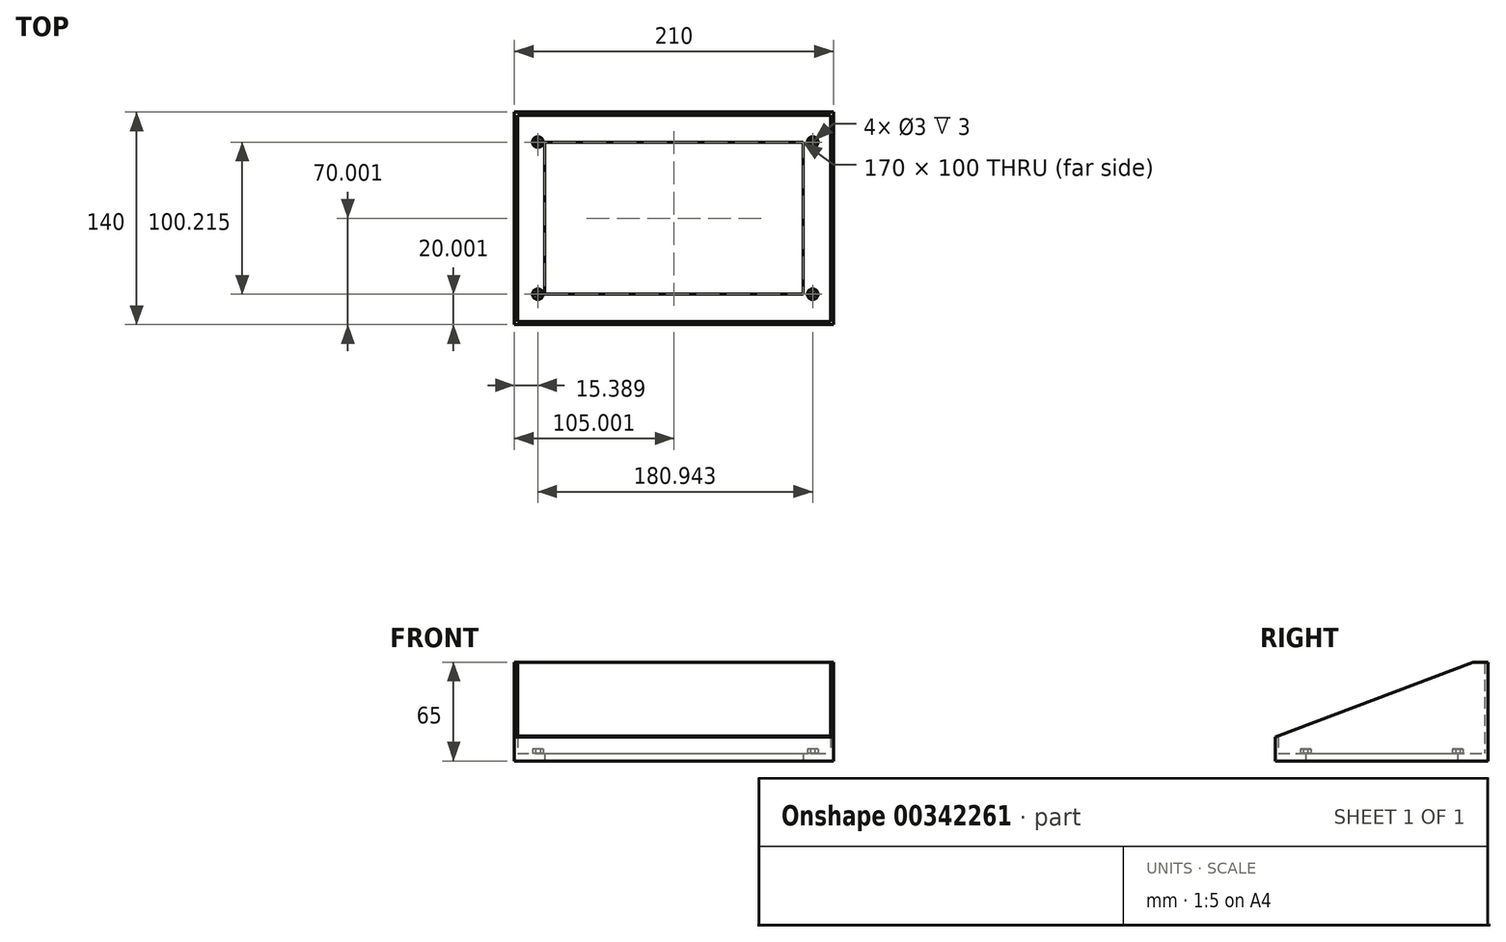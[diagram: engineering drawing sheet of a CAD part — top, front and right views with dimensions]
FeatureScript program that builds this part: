
annotation { "Feature Type Name" : "Feature", "Feature Type Description" : "" }
export const myFeature = defineFeature(function(context is Context, id is Id, definition is map)
    precondition{}
    {
        {
            var Q0;
            Q0=qCreatedBy(makeId("Top.planeOp"),FACE);
            var sketch = newSketch(context, id + "F0", { "sketchPlane" : qUnion([Q0])});
            skLineSegment(sketch, "E0.bottom", {"start": v(-80.08, -50.32) * mm, "end": v(89.92, -50.32) * mm});
            skLineSegment(sketch, "E0.top", {"start": v(-80.08, 49.68) * mm, "end": v(89.92, 49.68) * mm});
            skLineSegment(sketch, "E0.left", {"start": v(-80.08, -50.32) * mm, "end": v(-80.08, 49.68) * mm});
            skLineSegment(sketch, "E0.right", {"start": v(89.92, -50.32) * mm, "end": v(89.92, 49.68) * mm});
            skLineSegment(sketch, "E1.0", {"start": v(-100.08, 69.68) * mm, "end": v(109.92, 69.68) * mm});
            skLineSegment(sketch, "E1.1", {"start": v(-100.08, -70.32) * mm, "end": v(-100.08, 69.68) * mm});
            skLineSegment(sketch, "E1.2", {"start": v(-100.08, -70.32) * mm, "end": v(109.92, -70.32) * mm});
            skLineSegment(sketch, "E1.3", {"start": v(109.92, -70.32) * mm, "end": v(109.92, 69.68) * mm});
            skSolve(sketch);
        }
        {
            var Q0;
            Q0=makeQuery(id+"F0.imprint","IMPRINT",FACE,{"disambiguationData":[TD([[makeQuery(id+"F0.imprint","IMPRINT",EDGE,{"derivedFrom":sQuery(id+"F0.wireOp",EDGE,"E0.bottom")}),-1.0]])]});
            extrude(context, id + "F1", {"entities" : qUnion([Q0]), "depth" : 5 * mm});
        }
        {
            var Q0;
            Q0=makeQuery(id+"F1.opExtrude","CAP_FACE",FACE,{"disambiguationData":[OSD([sQuery(id+"F0.wireOp",EDGE,"E0.bottom"),sQuery(id+"F0.wireOp",EDGE,"E0.top"),sQuery(id+"F0.wireOp",EDGE,"E0.left"),sQuery(id+"F0.wireOp",EDGE,"E0.right"),sQuery(id+"F0.wireOp",EDGE,"E1.0"),sQuery(id+"F0.wireOp",EDGE,"E1.1"),sQuery(id+"F0.wireOp",EDGE,"E1.2"),sQuery(id+"F0.wireOp",EDGE,"E1.3")])],"isStart":false});
            var sketch = newSketch(context, id + "F2", { "sketchPlane" : qUnion([Q0])});
            skPoint(sketch, "E2", {"position": v(-84.7, 49.9) * mm});
            skPoint(sketch, "E3", {"position": v(96.25, 49.9) * mm});
            skPoint(sketch, "E4", {"position": v(96.25, -50.32) * mm});
            skPoint(sketch, "E5", {"position": v(-84.7, -50.32) * mm});
            skLineSegment(sketch, "E6.0", {"start": v(-98.08, -68.32) * mm, "end": v(-98.08, 67.68) * mm});
            skLineSegment(sketch, "E6.1", {"start": v(-98.08, -68.32) * mm, "end": v(107.92, -68.32) * mm});
            skLineSegment(sketch, "E6.2", {"start": v(107.92, -68.32) * mm, "end": v(107.92, 67.68) * mm});
            skLineSegment(sketch, "E6.3", {"start": v(-98.08, 67.68) * mm, "end": v(107.92, 67.68) * mm});
            skCircle(sketch, "E7", {"center": v(-84.7, 49.9) * mm, "radius": 3.5 * mm});
            skCircle(sketch, "E8", {"center": v(96.25, 49.9) * mm, "radius": 3.5 * mm});
            skCircle(sketch, "E9", {"center": v(96.25, -50.32) * mm, "radius": 3.5 * mm});
            skCircle(sketch, "E10", {"center": v(-84.7, -50.32) * mm, "radius": 3.5 * mm});
            skSolve(sketch);
        }
        {
            var Q0;
            Q0=makeQuery(id+"F2.imprint","IMPRINT",FACE,{"disambiguationData":[TD([[makeQuery(id+"F2.imprint","IMPRINT",EDGE,{"derivedFrom":sQuery(id+"F2.wireOp",EDGE,"E6.0")}),1.0]])]});
            extrude(context, id + "F3", {"entities" : qUnion([Q0]), "operationType" : NewBodyOperationType.ADD, "depth" : 60 * mm});
        }
        {
            var Q0;
            Q0=makeQuery(id+"F2.imprint","IMPRINT",FACE,{"disambiguationData":[TD([[makeQuery(id+"F2.imprint","IMPRINT",EDGE,{"derivedFrom":sQuery(id+"F2.wireOp",EDGE,"E7")}),1.0]])]});
            var Q1;
            Q1=makeQuery(id+"F2.imprint","IMPRINT",FACE,{"disambiguationData":[TD([[makeQuery(id+"F2.imprint","IMPRINT",EDGE,{"derivedFrom":sQuery(id+"F2.wireOp",EDGE,"E8")}),1.0]])]});
            var Q2;
            Q2=makeQuery(id+"F2.imprint","IMPRINT",FACE,{"disambiguationData":[TD([[makeQuery(id+"F2.imprint","IMPRINT",EDGE,{"derivedFrom":sQuery(id+"F2.wireOp",EDGE,"E10")}),1.0]])]});
            var Q3;
            Q3=makeQuery(id+"F2.imprint","IMPRINT",FACE,{"disambiguationData":[TD([[makeQuery(id+"F2.imprint","IMPRINT",EDGE,{"derivedFrom":sQuery(id+"F2.wireOp",EDGE,"E9")}),1.0]])]});
            var Q4;
            Q4=sQuery(id+"F2.wireOp",EDGE,"E7");
            var Q5;
            Q5=sQuery(id+"F2.wireOp",EDGE,"E8");
            var Q6;
            Q6=sQuery(id+"F2.wireOp",EDGE,"E9");
            var Q7;
            Q7=sQuery(id+"F2.wireOp",EDGE,"E10");
            extrude(context, id + "F4", {"entities" : qUnion([Q0, Q1, Q2, Q3]), "operationType" : NewBodyOperationType.ADD, "surfaceEntities" : qUnion([Q4, Q5, Q6, Q7]), "depth" : 3 * mm});
        }
        {
            var Q0;
            Q0=sQuery(id+"F2.wireOp",VERTEX,"E2");
            var Q1;
            Q1=sQuery(id+"F2.wireOp",VERTEX,"E3");
            var Q2;
            Q2=sQuery(id+"F2.wireOp",VERTEX,"E5");
            var Q3;
            Q3=sQuery(id+"F2.wireOp",VERTEX,"E4");
            var Q4;
            Q4=makeQuery(id+"F1.opExtrude","SWEPT_BODY",BODY,{"disambiguationData":[OSD([sQuery(id+"F0.wireOp",EDGE,"E0.bottom"),sQuery(id+"F0.wireOp",EDGE,"E0.top"),sQuery(id+"F0.wireOp",EDGE,"E0.left"),sQuery(id+"F0.wireOp",EDGE,"E0.right"),sQuery(id+"F0.wireOp",EDGE,"E1.0"),sQuery(id+"F0.wireOp",EDGE,"E1.1"),sQuery(id+"F0.wireOp",EDGE,"E1.2"),sQuery(id+"F0.wireOp",EDGE,"E1.3")])]});
            hole(context, id + "F5", {"style" : HoleStyle.SIMPLE, "endStyle" : HoleEndStyle.BLIND, "oppositeDirection" : true, "holeDiameter" : 3 * mm, "holeDepth" : 15 * mm, "isTappedThrough" : true, "tappedDepth" : 12 * mm, "tapClearance" : 3, "startFromSketch" : true, "locations" : qUnion([Q0, Q1, Q2, Q3]), "scope" : qUnion([Q4])});
        }
        {
            var Q0;
            {var subQ0=sQuery(id+"F0.wireOp",EDGE,"E1.3");Q0=makeQuery(id+"F3.boolean.opBoolean","MERGE",FACE,{"derivedFrom":[makeQuery(id+"F1.opExtrude","SWEPT_FACE",FACE,{"disambiguationData":[OSD([subQ0])]}),makeQuery(id+"F3.opExtrude","SWEPT_FACE",FACE,{"disambiguationData":[OSD([subQ0])]})]});}
            var sketch = newSketch(context, id + "F6", { "sketchPlane" : qUnion([Q0])});
            skLineSegment(sketch, "E11", {"start": v(80.17, 72.68) * mm, "end": v(-94.78, 6.45) * mm});
            skLineSegment(sketch, "E12", {"start": v(-94.78, 6.45) * mm, "end": v(-94.78, 76.66) * mm});
            skLineSegment(sketch, "E13", {"start": v(-94.78, 76.66) * mm, "end": v(80.17, 72.68) * mm});
            skSolve(sketch);
        }
        {
            var Q0;
            Q0 = qSketchRegion(id + "F6", true);
            extrude(context, id + "F7", {"entities" : qUnion([Q0]), "operationType" : NewBodyOperationType.REMOVE, "oppositeDirection" : true, "depth" : 300 * mm});
        }
    });
